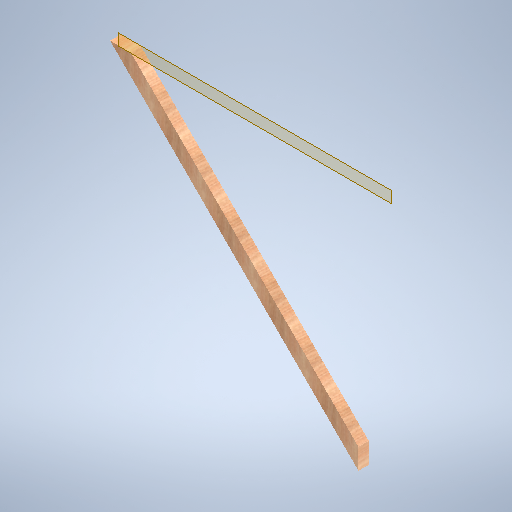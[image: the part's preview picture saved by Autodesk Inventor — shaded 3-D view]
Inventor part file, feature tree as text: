
AUTODESK INVENTOR PART (.ipt)
format: ipt  version: 2025 (Build 290162000, 162)  size: 292,864 bytes
history: native  units: in
note: dims shown in document units (in); Inventor stores cm internally (conversion verified against a paired STEP export)
features: other x3, plane x1, extrude x1, sketch x1
ambient origin geometry x8: Origin, YZ Plane, XZ Plane, XY Plane, X Axis, Y Axis, Z Axis, Center Point
bodies: Solid1 (feature_tree)
feature tree (6):
  plane  "Work Plane1"
  extrude  "Extrusion1"  Depth=2.0in
  sketch  "Sketch1"  dims[d1=4.0in d2=65.0in d4=4.0in d5=2.0in d6=0.0in]
  other  "<userpath>\Documents\GitHub\USCTigerBurn24\v2\Tiger.iam"
  other  "Tiger.iam"
  other  "2x4x48:12"
